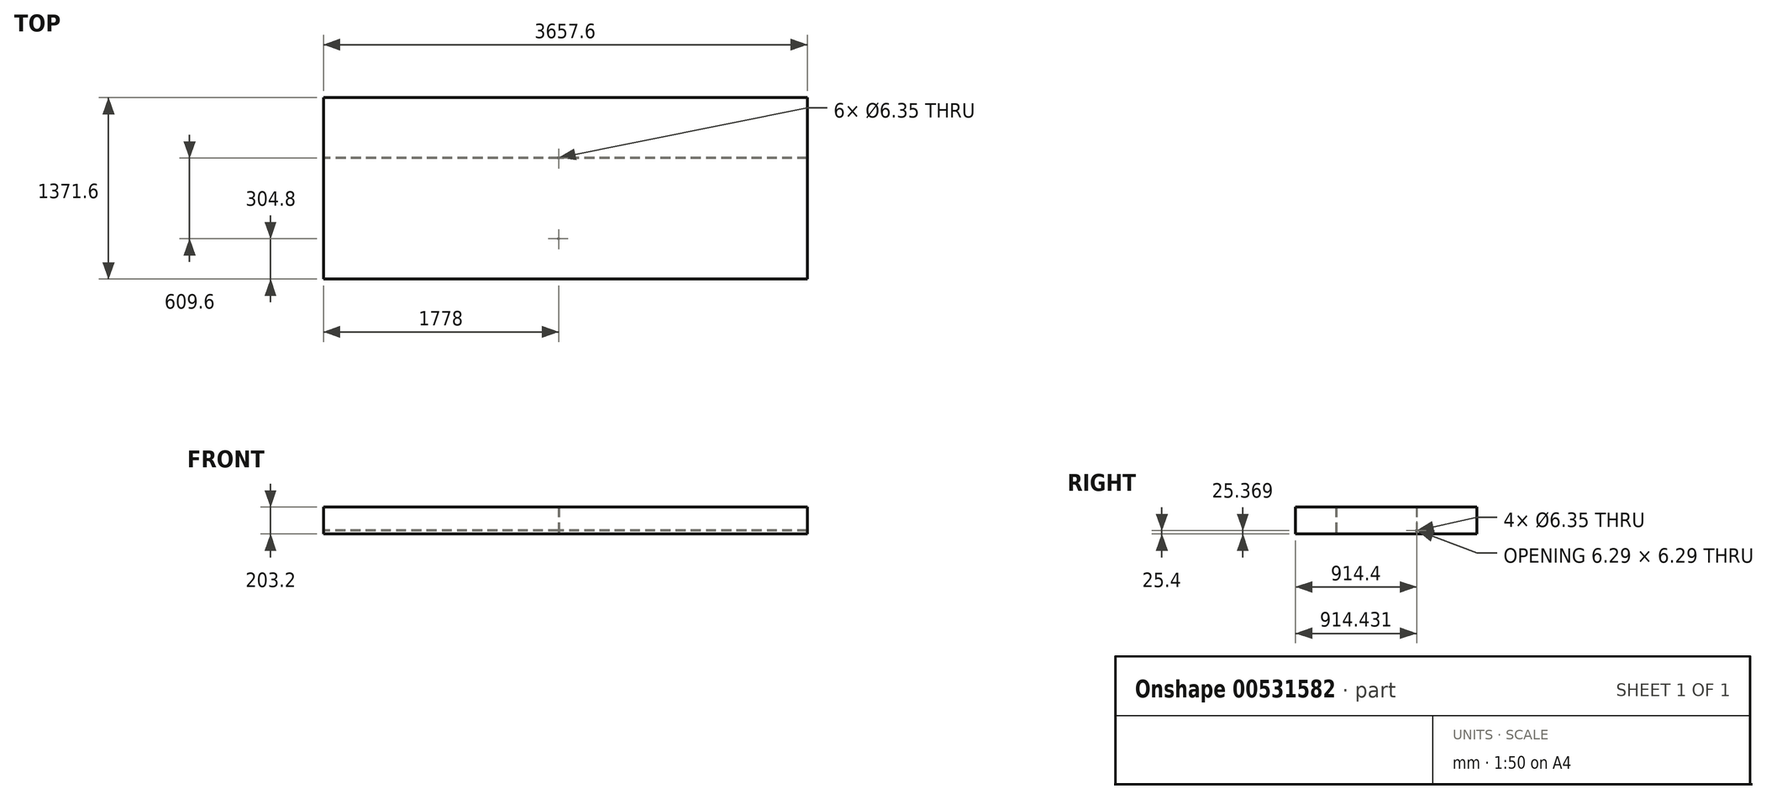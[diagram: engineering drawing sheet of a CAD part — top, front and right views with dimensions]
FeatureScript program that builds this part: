
annotation { "Feature Type Name" : "Feature", "Feature Type Description" : "" }
export const myFeature = defineFeature(function(context is Context, id is Id, definition is map)
    precondition{}
    {
        {
            var Q0;
            Q0=qCreatedBy(makeId("Front.planeOp"),FACE);
            var sketch = newSketch(context, id + "F0", { "sketchPlane" : qUnion([Q0])});
            skLineSegment(sketch, "E0.bottom", {"start": v(0, 0) * mm, "end": v(3657.6, 0) * mm});
            skLineSegment(sketch, "E0.top", {"start": v(0, 203.2) * mm, "end": v(3657.6, 203.2) * mm});
            skLineSegment(sketch, "E0.left", {"start": v(0, 0) * mm, "end": v(0, 203.2) * mm});
            skLineSegment(sketch, "E0.right", {"start": v(3657.6, 0) * mm, "end": v(3657.6, 203.2) * mm});
            skSolve(sketch);
        }
        {
            var Q0;
            Q0=qCreatedBy(makeId("Right.planeOp"),FACE);
            var sketch = newSketch(context, id + "F1", { "sketchPlane" : qUnion([Q0])});
            skLineSegment(sketch, "E1.bottom", {"start": v(0, 0) * mm, "end": v(1371.6, 0) * mm});
            skLineSegment(sketch, "E1.top", {"start": v(0, 203.2) * mm, "end": v(1371.6, 203.2) * mm});
            skLineSegment(sketch, "E1.left", {"start": v(0, 0) * mm, "end": v(0, 203.2) * mm});
            skLineSegment(sketch, "E1.right", {"start": v(1371.6, 0) * mm, "end": v(1371.6, 203.2) * mm});
            skPoint(sketch, "E2", {"position": v(914.4, 25.4) * mm});
            skSolve(sketch);
        }
        {
            var Q0;
            Q0=qCreatedBy(makeId("Top.planeOp"),FACE);
            var sketch = newSketch(context, id + "F2", { "sketchPlane" : qUnion([Q0])});
            skLineSegment(sketch, "E3.bottom", {"start": v(0, 0) * mm, "end": v(3657.6, 0) * mm});
            skLineSegment(sketch, "E3.top", {"start": v(0, 1371.6) * mm, "end": v(3657.6, 1371.6) * mm});
            skLineSegment(sketch, "E3.left", {"start": v(0, 0) * mm, "end": v(0, 1371.6) * mm});
            skLineSegment(sketch, "E3.right", {"start": v(3657.6, 0) * mm, "end": v(3657.6, 1371.6) * mm});
            skPoint(sketch, "E4", {"position": v(1778, 304.8) * mm});
            skPoint(sketch, "E5", {"position": v(1778, 914.4) * mm});
            skSolve(sketch);
        }
        {
            var Q0;
            Q0=makeQuery(id+"F0.imprint","IMPRINT",FACE,{"disambiguationData":[TD([[makeQuery(id+"F0.imprint","IMPRINT",EDGE,{"derivedFrom":sQuery(id+"F0.wireOp",EDGE,"E0.bottom")}),1.0]])]});
            extrude(context, id + "F3", {"entities" : qUnion([Q0]), "oppositeDirection" : true, "depth" : 1371.6 * mm, "offsetDistance" : 25.4 * mm});
        }
        {
            var Q0;
            Q0=sQuery(id+"F1.wireOp",VERTEX,"E2");
            var Q1;
            Q1=makeQuery(id+"F3.opExtrude","SWEPT_BODY",BODY,{"disambiguationData":[OSD([sQuery(id+"F0.wireOp",EDGE,"E0.bottom"),sQuery(id+"F0.wireOp",EDGE,"E0.top"),sQuery(id+"F0.wireOp",EDGE,"E0.left"),sQuery(id+"F0.wireOp",EDGE,"E0.right")])]});
            hole(context, id + "F4", {"style" : HoleStyle.SIMPLE, "endStyle" : HoleEndStyle.THROUGH, "oppositeDirection" : true, "holeDiameter" : 6.35 * mm, "isTappedThrough" : true, "tappedDepth" : 12.7 * mm, "tapClearance" : 3, "locations" : qUnion([Q0]), "scope" : qUnion([Q1])});
        }
        {
            var Q0;
            Q0=sQuery(id+"F2.wireOp",VERTEX,"E4");
            var Q1;
            Q1=makeQuery(id+"F3.opExtrude","SWEPT_BODY",BODY,{"disambiguationData":[OSD([sQuery(id+"F0.wireOp",EDGE,"E0.bottom"),sQuery(id+"F0.wireOp",EDGE,"E0.top"),sQuery(id+"F0.wireOp",EDGE,"E0.left"),sQuery(id+"F0.wireOp",EDGE,"E0.right")])]});
            hole(context, id + "F5", {"style" : HoleStyle.SIMPLE, "endStyle" : HoleEndStyle.THROUGH, "oppositeDirection" : true, "holeDiameter" : 6.35 * mm, "isTappedThrough" : true, "tappedDepth" : 12.7 * mm, "tapClearance" : 3, "locations" : qUnion([Q0]), "scope" : qUnion([Q1])});
        }
        {
            var Q0;
            Q0=sQuery(id+"F2.wireOp",VERTEX,"E5");
            var Q1;
            Q1=makeQuery(id+"F3.opExtrude","SWEPT_BODY",BODY,{"disambiguationData":[OSD([sQuery(id+"F0.wireOp",EDGE,"E0.bottom"),sQuery(id+"F0.wireOp",EDGE,"E0.top"),sQuery(id+"F0.wireOp",EDGE,"E0.left"),sQuery(id+"F0.wireOp",EDGE,"E0.right")])]});
            hole(context, id + "F6", {"style" : HoleStyle.SIMPLE, "endStyle" : HoleEndStyle.THROUGH, "oppositeDirection" : true, "holeDiameter" : 6.35 * mm, "isTappedThrough" : true, "tappedDepth" : 12.7 * mm, "tapClearance" : 3, "locations" : qUnion([Q0]), "scope" : qUnion([Q1])});
        }
    });
